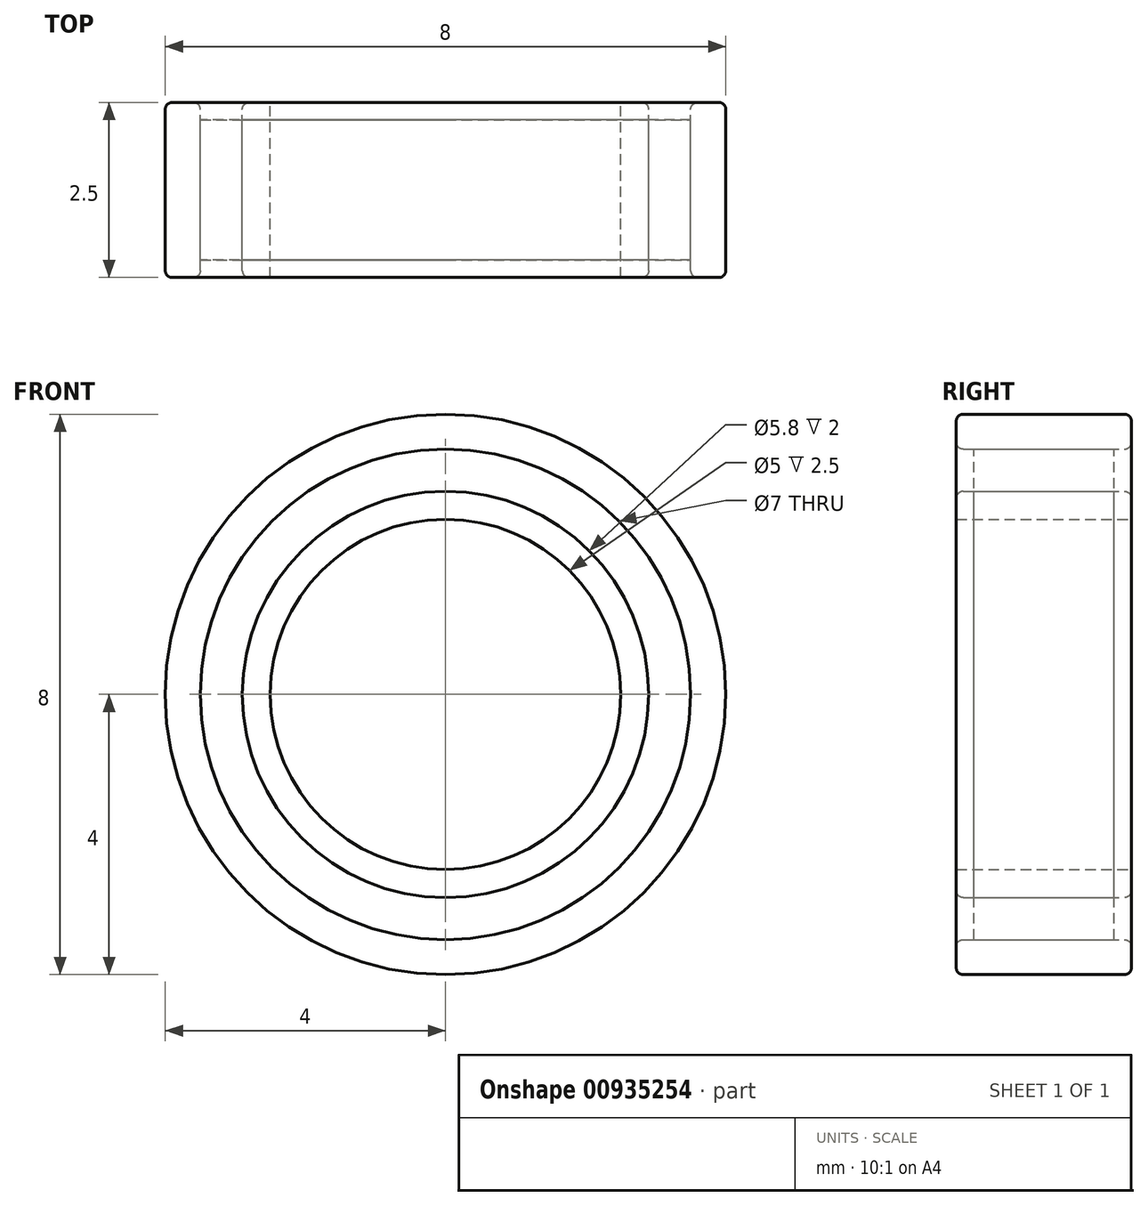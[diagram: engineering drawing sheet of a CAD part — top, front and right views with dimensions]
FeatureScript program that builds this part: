
annotation { "Feature Type Name" : "Feature", "Feature Type Description" : "" }
export const myFeature = defineFeature(function(context is Context, id is Id, definition is map)
    precondition{}
    {
        {
            var Q0;
            Q0=qCreatedBy(makeId("Front.planeOp"),FACE);
            var sketch = newSketch(context, id + "F0", { "sketchPlane" : qUnion([Q0])});
            skCircle(sketch, "E0", {"center": v(0, 0) * mm, "radius": 2.5 * mm});
            skCircle(sketch, "E1", {"center": v(0, 0) * mm, "radius": 4 * mm});
            skCircle(sketch, "E2", {"center": v(0, 0) * mm, "radius": 2.9 * mm});
            skCircle(sketch, "E3", {"center": v(0, 0) * mm, "radius": 3.5 * mm});
            skSolve(sketch);
        }
        {
            var Q0;
            Q0=makeQuery(id+"F0.imprint","IMPRINT",FACE,{"disambiguationData":[TD([[makeQuery(id+"F0.imprint","IMPRINT",EDGE,{"derivedFrom":sQuery(id+"F0.wireOp",EDGE,"E0")}),-1.0]])]});
            var Q1;
            Q1=makeQuery(id+"F0.imprint","IMPRINT",FACE,{"disambiguationData":[TD([[makeQuery(id+"F0.imprint","IMPRINT",EDGE,{"derivedFrom":sQuery(id+"F0.wireOp",EDGE,"E1")}),1.0]])]});
            extrude(context, id + "F1", {"entities" : qUnion([Q0, Q1]), "endBound" : BoundingType.SYMMETRIC, "depth" : 2.5 * mm, "offsetDistance" : 25 * mm});
        }
        {
            var Q0;
            Q0=makeQuery(id+"F0.imprint","IMPRINT",FACE,{"disambiguationData":[TD([[makeQuery(id+"F0.imprint","IMPRINT",EDGE,{"derivedFrom":sQuery(id+"F0.wireOp",EDGE,"E2")}),-1.0]])]});
            extrude(context, id + "F2", {"entities" : qUnion([Q0]), "endBound" : BoundingType.SYMMETRIC, "depth" : 2 * mm, "offsetDistance" : 25 * mm});
        }
        {
            var Q0;
            Q0=makeQuery(id+"F1.opExtrude","CAP_EDGE",EDGE,{"disambiguationData":[OSD([sQuery(id+"F0.wireOp",EDGE,"E2")])],"isStart":true});
            var Q1;
            Q1=makeQuery(id+"F1.opExtrude","CAP_EDGE",EDGE,{"disambiguationData":[OSD([sQuery(id+"F0.wireOp",EDGE,"E1")])],"isStart":true});
            var Q2;
            Q2=makeQuery(id+"F1.opExtrude","CAP_EDGE",EDGE,{"disambiguationData":[OSD([sQuery(id+"F0.wireOp",EDGE,"E3")])],"isStart":true});
            var Q3;
            Q3=makeQuery(id+"F1.opExtrude","CAP_EDGE",EDGE,{"disambiguationData":[OSD([sQuery(id+"F0.wireOp",EDGE,"E1")])],"isStart":false});
            var Q4;
            Q4=makeQuery(id+"F1.opExtrude","CAP_EDGE",EDGE,{"disambiguationData":[OSD([sQuery(id+"F0.wireOp",EDGE,"E3")])],"isStart":false});
            var Q5;
            Q5=makeQuery(id+"F1.opExtrude","CAP_EDGE",EDGE,{"disambiguationData":[OSD([sQuery(id+"F0.wireOp",EDGE,"E2")])],"isStart":false});
            fillet(context, id + "F3", {"entities" : qUnion([Q0, Q1, Q2, Q3, Q4, Q5]), "radius" : 0.1 * mm, "tangentPropagation" : true, "allowEdgeOverflow" : false});
        }
    });
